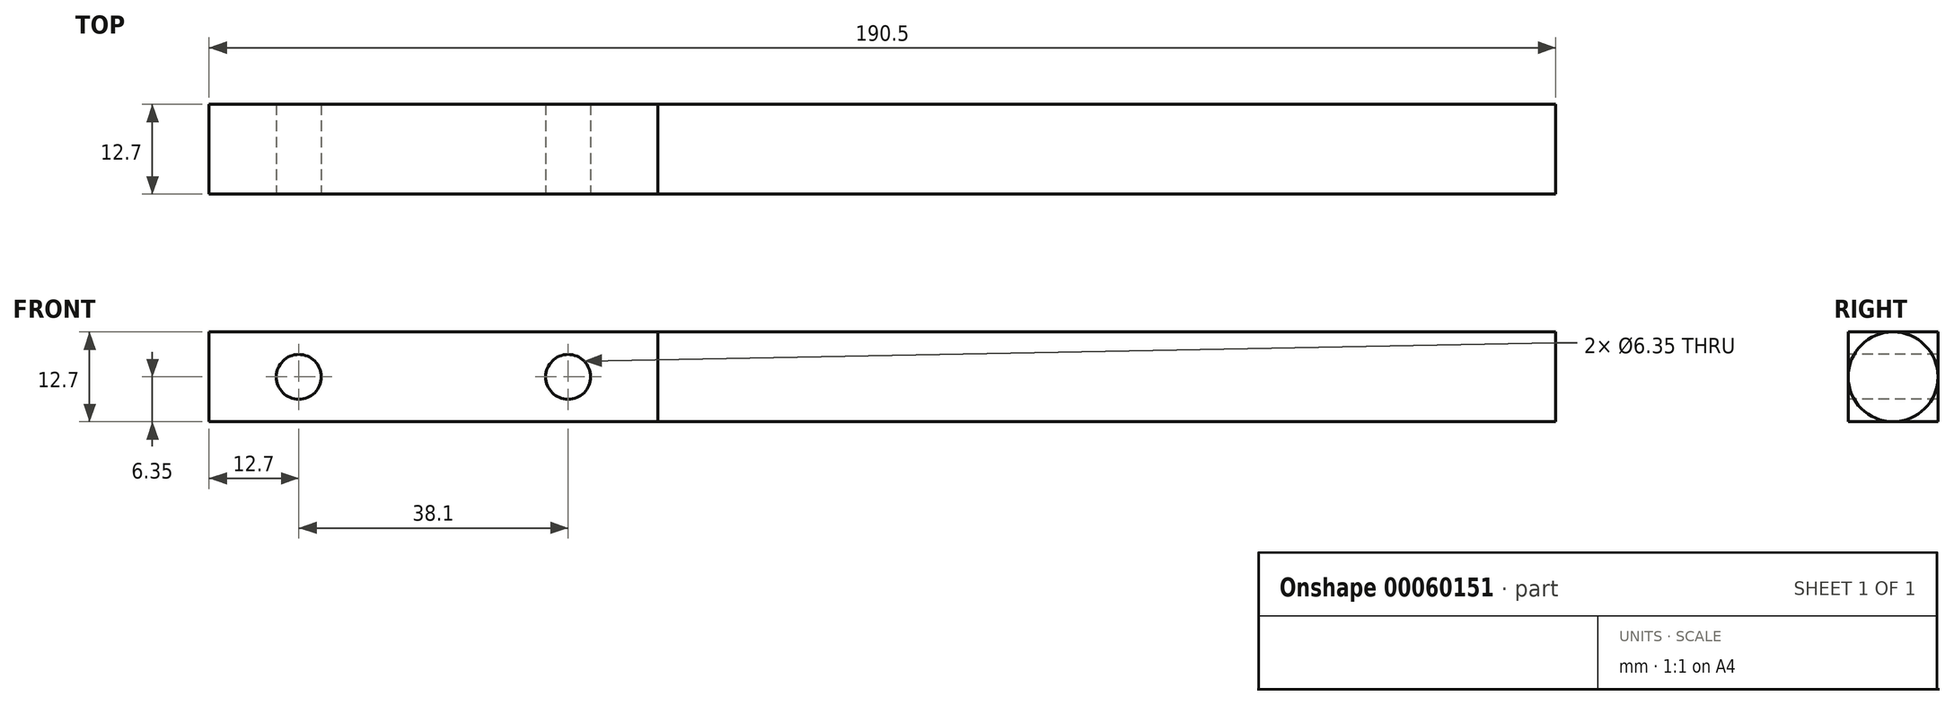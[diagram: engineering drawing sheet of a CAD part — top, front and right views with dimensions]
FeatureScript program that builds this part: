
annotation { "Feature Type Name" : "Feature", "Feature Type Description" : "" }
export const myFeature = defineFeature(function(context is Context, id is Id, definition is map)
    precondition{}
    {
        {
            var Q0;
            Q0=qCreatedBy(makeId("Right.planeOp"),FACE);
            var sketch = newSketch(context, id + "F0", { "sketchPlane" : qUnion([Q0])});
            skLineSegment(sketch, "E0.rect.bottom", {"start": v(6.35, -6.35) * mm, "end": v(-6.35, -6.35) * mm});
            skLineSegment(sketch, "E0.rect.top", {"start": v(6.35, 6.35) * mm, "end": v(-6.35, 6.35) * mm});
            skLineSegment(sketch, "E0.rect.left", {"start": v(6.35, -6.35) * mm, "end": v(6.35, 6.35) * mm});
            skLineSegment(sketch, "E0.rect.right", {"start": v(-6.35, -6.35) * mm, "end": v(-6.35, 6.35) * mm});
            skPoint(sketch, "E0.rect.middle", {"position": v(0, 0) * mm});
            skSolve(sketch);
        }
        {
            var Q0;
            Q0=makeQuery(id+"F0.imprint","IMPRINT",FACE,{"disambiguationData":[TD([[makeQuery(id+"F0.imprint","IMPRINT",EDGE,{"derivedFrom":sQuery(id+"F0.wireOp",EDGE,"E0.rect.bottom")}),-1.0]])]});
            extrude(context, id + "F1", {"entities" : qUnion([Q0]), "oppositeDirection" : true, "depth" : 63.5 * mm});
        }
        {
            var Q0;
            Q0=makeQuery(id+"F1.opExtrude","CAP_FACE",FACE,{"disambiguationData":[OSD([sQuery(id+"F0.wireOp",EDGE,"E0.rect.bottom"),sQuery(id+"F0.wireOp",EDGE,"E0.rect.top"),sQuery(id+"F0.wireOp",EDGE,"E0.rect.left"),sQuery(id+"F0.wireOp",EDGE,"E0.rect.right")])],"isStart":true});
            var sketch = newSketch(context, id + "F2", { "sketchPlane" : qUnion([Q0])});
            skCircle(sketch, "E1", {"center": v(0, 0) * mm, "radius": 6.35 * mm});
            skSolve(sketch);
        }
        {
            var Q0;
            Q0 = qSketchRegion(id + "F2", true);
            extrude(context, id + "F3", {"entities" : qUnion([Q0]), "operationType" : NewBodyOperationType.ADD, "depth" : 127 * mm});
        }
        {
            var Q0;
            Q0=makeQuery(id+"F1.opExtrude","SWEPT_FACE",FACE,{"disambiguationData":[OSD([sQuery(id+"F0.wireOp",EDGE,"E0.rect.right")])]});
            var sketch = newSketch(context, id + "F4", { "sketchPlane" : qUnion([Q0])});
            skCircle(sketch, "E2", {"center": v(-50.8, 0) * mm, "radius": 3.18 * mm});
            skCircle(sketch, "E3", {"center": v(-12.7, 0) * mm, "radius": 3.18 * mm});
            skSolve(sketch);
        }
        {
            var Q0;
            Q0 = qSketchRegion(id + "F4", true);
            extrude(context, id + "F5", {"entities" : qUnion([Q0]), "operationType" : NewBodyOperationType.REMOVE, "oppositeDirection" : true, "depth" : 25.4 * mm});
        }
    });
